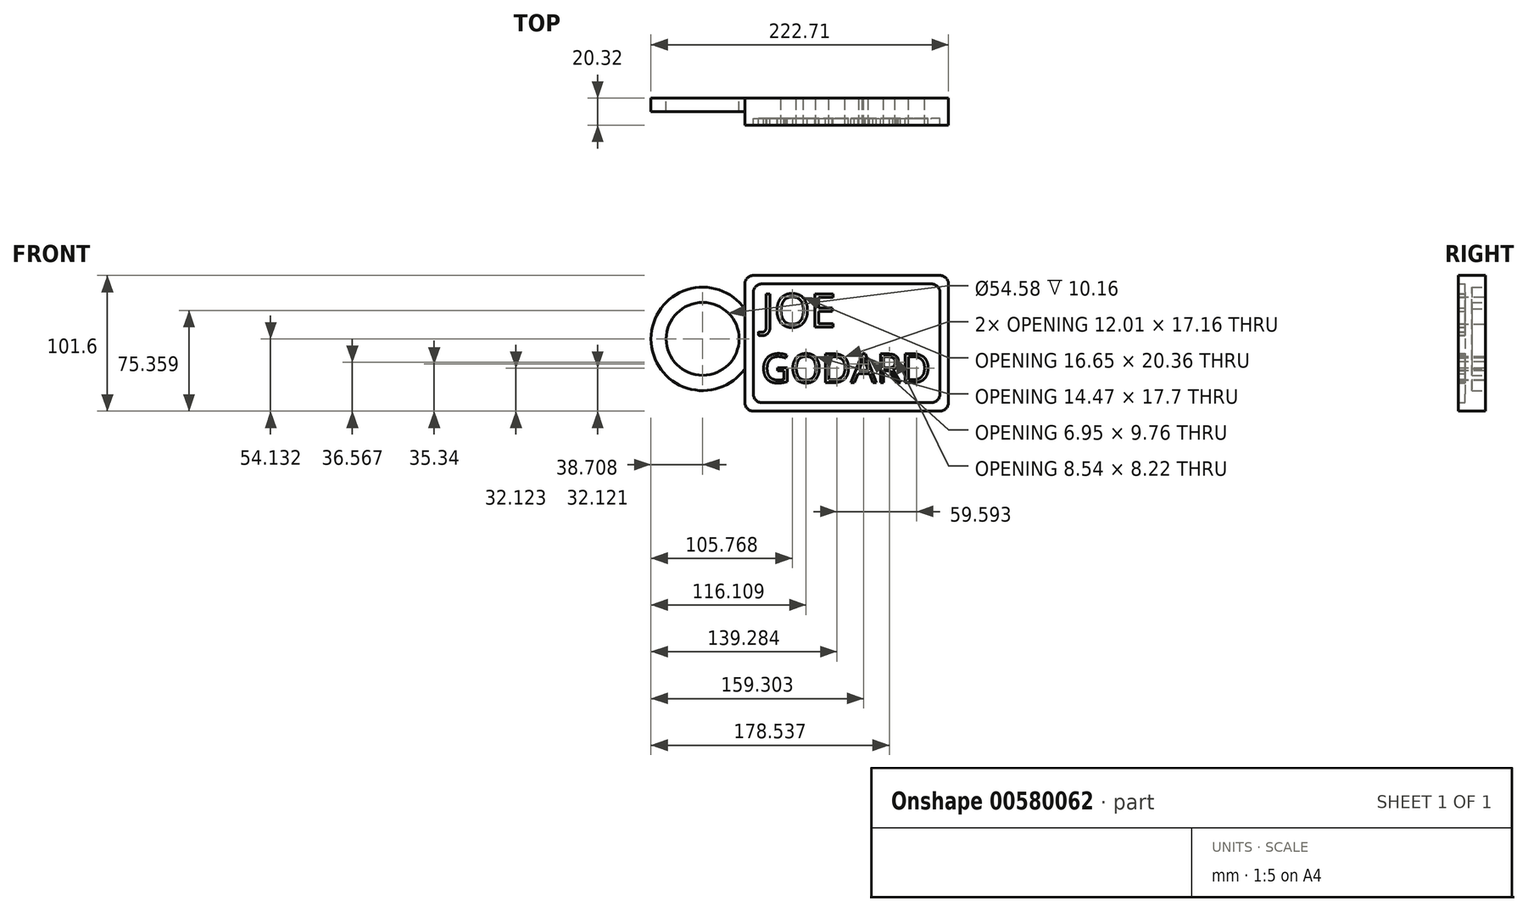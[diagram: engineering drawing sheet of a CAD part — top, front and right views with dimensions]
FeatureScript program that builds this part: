
annotation { "Feature Type Name" : "Feature", "Feature Type Description" : "" }
export const myFeature = defineFeature(function(context is Context, id is Id, definition is map)
    precondition{}
    {
        {
            var Q0;
            Q0=qCreatedBy(makeId("Front.planeOp"),FACE);
            var sketch = newSketch(context, id + "F0", { "sketchPlane" : qUnion([Q0])});
            skLineSegment(sketch, "E0.bottom", {"start": v(6.35, 0) * mm, "end": v(146.05, 0) * mm});
            skLineSegment(sketch, "E0.top", {"start": v(6.35, 101.6) * mm, "end": v(146.05, 101.6) * mm});
            skLineSegment(sketch, "E0.left", {"start": v(0, 6.35) * mm, "end": v(0, 31.78) * mm});
            skLineSegment(sketch, "E0.right", {"start": v(152.4, 6.35) * mm, "end": v(152.4, 95.25) * mm});
            skText(sketch, "E1", { "text": "JOE", "fontName": "OpenSans-Regular.ttf"});
            skText(sketch, "E2", { "text": "GODARD", "fontName": "OpenSans-Regular.ttf"});
            skArc(sketch, "E3", {"start": v(0, 76.48) * mm, "mid": v(-70.3, 54.13) * mm, "end": v(0, 31.78) * mm});
            skCircle(sketch, "E4", {"center": v(-31.6, 54.13) * mm, "radius": 27.3 * mm});
            skLineSegment(sketch, "E5.trimOffspring", {"start": v(0, 76.48) * mm, "end": v(0, 95.25) * mm});
            skPoint(sketch, "E6.visualSharp", {"position": v(0, 101.6) * mm});
            skArc(sketch, "E6.filletArc", {"start": v(6.35, 101.6) * mm, "mid": v(1.86, 99.74) * mm, "end": v(0, 95.25) * mm});
            skPoint(sketch, "E7.visualSharp", {"position": v(152.4, 101.6) * mm});
            skArc(sketch, "E7.filletArc", {"start": v(152.4, 95.25) * mm, "mid": v(150.54, 99.74) * mm, "end": v(146.05, 101.6) * mm});
            skPoint(sketch, "E8.visualSharp", {"position": v(152.4, 0) * mm});
            skArc(sketch, "E8.filletArc", {"start": v(146.05, 0) * mm, "mid": v(150.54, 1.86) * mm, "end": v(152.4, 6.35) * mm});
            skPoint(sketch, "E9.visualSharp", {"position": v(0, 0) * mm});
            skArc(sketch, "E9.filletArc", {"start": v(0, 6.35) * mm, "mid": v(1.86, 1.86) * mm, "end": v(6.35, 0) * mm});
            skLineSegment(sketch, "E10.bottom", {"start": v(12.7, 95.25) * mm, "end": v(139.7, 95.25) * mm});
            skLineSegment(sketch, "E10.top", {"start": v(12.7, 6.35) * mm, "end": v(139.7, 6.35) * mm});
            skLineSegment(sketch, "E10.left", {"start": v(6.35, 88.9) * mm, "end": v(6.35, 12.7) * mm});
            skLineSegment(sketch, "E10.right", {"start": v(146.05, 88.9) * mm, "end": v(146.05, 12.7) * mm});
            skArc(sketch, "E11.filletArc", {"start": v(12.7, 95.25) * mm, "mid": v(8.2, 93.4) * mm, "end": v(6.35, 88.9) * mm});
            skArc(sketch, "E12.filletArc", {"start": v(146.05, 88.9) * mm, "mid": v(144.2, 93.4) * mm, "end": v(139.7, 95.25) * mm});
            skArc(sketch, "E13.filletArc", {"start": v(139.7, 6.35) * mm, "mid": v(144.2, 8.2) * mm, "end": v(146.05, 12.7) * mm});
            skArc(sketch, "E14.filletArc", {"start": v(6.35, 12.7) * mm, "mid": v(8.2, 8.2) * mm, "end": v(12.7, 6.35) * mm});
            skLineSegment(sketch, "E15", {"start": v(0, 76.48) * mm, "end": v(0, 31.78) * mm});
            const initialGuessF0  = {"E1": [0.01273, 0.063, 1, 0, 0.02493], "E2": [0.01217, 0.02138, 1, 0, 0.02167]};
            skSetInitialGuess(sketch, initialGuessF0);
            skSolve(sketch);
        }
        {
            var Q0;
            Q0=makeQuery(id+"F0.imprint","IMPRINT",FACE,{"disambiguationData":[TD([[makeQuery(id+"F0.imprint","IMPRINT",EDGE,{"derivedFrom":sQuery(id+"F0.wireOp",EDGE,"E0.bottom")}),1.0]])]});
            extrude(context, id + "F1", {"entities" : qUnion([Q0]), "depth" : 20.32 * mm, "offsetDistance" : 25.4 * mm});
        }
        {
            var Q0;
            Q0=makeQuery(id+"F0.imprint","IMPRINT",FACE,{"disambiguationData":[TD([[makeQuery(id+"F0.imprint","IMPRINT",EDGE,{"derivedFrom":sQuery(id+"F0.wireOp",EDGE,"E1.sketch_text.stroke-0")}),1.0]])]});
            extrude(context, id + "F2", {"entities" : qUnion([Q0]), "operationType" : NewBodyOperationType.ADD, "depth" : 15.24 * mm, "offsetDistance" : 25.4 * mm});
        }
        {
            var Q0;
            Q0=makeQuery(id+"F0.imprint","IMPRINT",FACE,{"disambiguationData":[TD([[makeQuery(id+"F0.imprint","IMPRINT",EDGE,{"derivedFrom":sQuery(id+"F0.wireOp",EDGE,"E3")}),1.0]])]});
            extrude(context, id + "F3", {"entities" : qUnion([Q0]), "operationType" : NewBodyOperationType.ADD, "depth" : 10.16 * mm, "offsetDistance" : 25.4 * mm});
        }
        {
            var Q0;
            Q0=makeQuery(id+"F0.imprint","IMPRINT",FACE,{"disambiguationData":[TD([[makeQuery(id+"F0.imprint","IMPRINT",EDGE,{"derivedFrom":sQuery(id+"F0.wireOp",EDGE,"E1.sketch_text.stroke-10")}),-1.0]])]});
            var Q1;
            Q1=makeQuery(id+"F0.imprint","IMPRINT",FACE,{"disambiguationData":[TD([[makeQuery(id+"F0.imprint","IMPRINT",EDGE,{"derivedFrom":sQuery(id+"F0.wireOp",EDGE,"E1.sketch_text.stroke-0")}),-1.0]])]});
            var Q2;
            Q2=makeQuery(id+"F0.imprint","IMPRINT",FACE,{"disambiguationData":[TD([[makeQuery(id+"F0.imprint","IMPRINT",EDGE,{"derivedFrom":sQuery(id+"F0.wireOp",EDGE,"E1.sketch_text.stroke-26")}),-1.0]])]});
            var Q3;
            Q3=makeQuery(id+"F0.imprint","IMPRINT",FACE,{"disambiguationData":[TD([[makeQuery(id+"F0.imprint","IMPRINT",EDGE,{"derivedFrom":sQuery(id+"F0.wireOp",EDGE,"E2.sketch_text.stroke-0")}),-1.0]])]});
            var Q4;
            Q4=makeQuery(id+"F0.imprint","IMPRINT",FACE,{"disambiguationData":[TD([[makeQuery(id+"F0.imprint","IMPRINT",EDGE,{"derivedFrom":sQuery(id+"F0.wireOp",EDGE,"E2.sketch_text.stroke-20")}),-1.0]])]});
            var Q5;
            Q5=makeQuery(id+"F0.imprint","IMPRINT",FACE,{"disambiguationData":[TD([[makeQuery(id+"F0.imprint","IMPRINT",EDGE,{"derivedFrom":sQuery(id+"F0.wireOp",EDGE,"E2.sketch_text.stroke-36")}),-1.0]])]});
            var Q6;
            Q6=makeQuery(id+"F0.imprint","IMPRINT",FACE,{"disambiguationData":[TD([[makeQuery(id+"F0.imprint","IMPRINT",EDGE,{"derivedFrom":sQuery(id+"F0.wireOp",EDGE,"E2.sketch_text.stroke-50")}),-1.0]])]});
            var Q7;
            Q7=makeQuery(id+"F0.imprint","IMPRINT",FACE,{"disambiguationData":[TD([[makeQuery(id+"F0.imprint","IMPRINT",EDGE,{"derivedFrom":sQuery(id+"F0.wireOp",EDGE,"E2.sketch_text.stroke-63")}),-1.0]])]});
            var Q8;
            Q8=makeQuery(id+"F0.imprint","IMPRINT",FACE,{"disambiguationData":[TD([[makeQuery(id+"F0.imprint","IMPRINT",EDGE,{"derivedFrom":sQuery(id+"F0.wireOp",EDGE,"E2.sketch_text.stroke-81")}),-1.0]])]});
            extrude(context, id + "F4", {"entities" : qUnion([Q0, Q1, Q2, Q3, Q4, Q5, Q6, Q7, Q8]), "operationType" : NewBodyOperationType.ADD, "depth" : 20.32 * mm, "offsetDistance" : 25.4 * mm});
        }
    });
